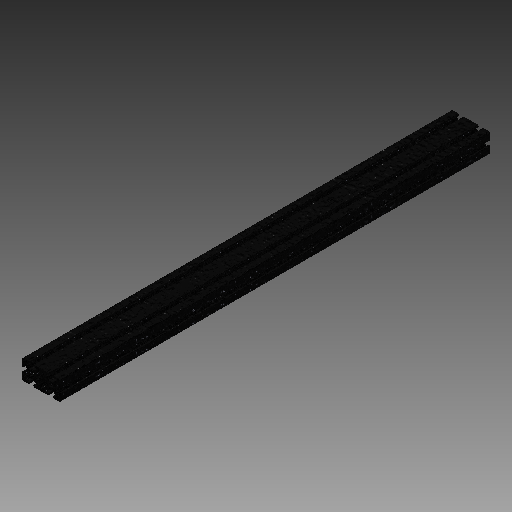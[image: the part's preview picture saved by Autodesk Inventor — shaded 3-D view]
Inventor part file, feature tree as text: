
AUTODESK INVENTOR PART (.ipt)
format: ipt  version: 2019 (Build 230136000, 136)  size: 346,112 bytes
history: native  units: in
note: dims shown in document units (in); Inventor stores cm internally (conversion verified against a paired STEP export)
features: extrude x1, sketch x1
ambient origin geometry x8: Origin, YZ Plane, XZ Plane, XY Plane, X Axis, Y Axis, Z Axis, Center Point
bodies: Solid1 (feature_tree)
feature tree (2):
  extrude  "Extrusion1"  [1 undecoded]
  sketch  "Sketch1"  dims[d0=33.0in d1=0.0in]
note: 1 required parameter value undecoded (feature->parameter linkage not recoverable at this tier; creation-order binding heuristic only, values carry confidence <= 0.55)
